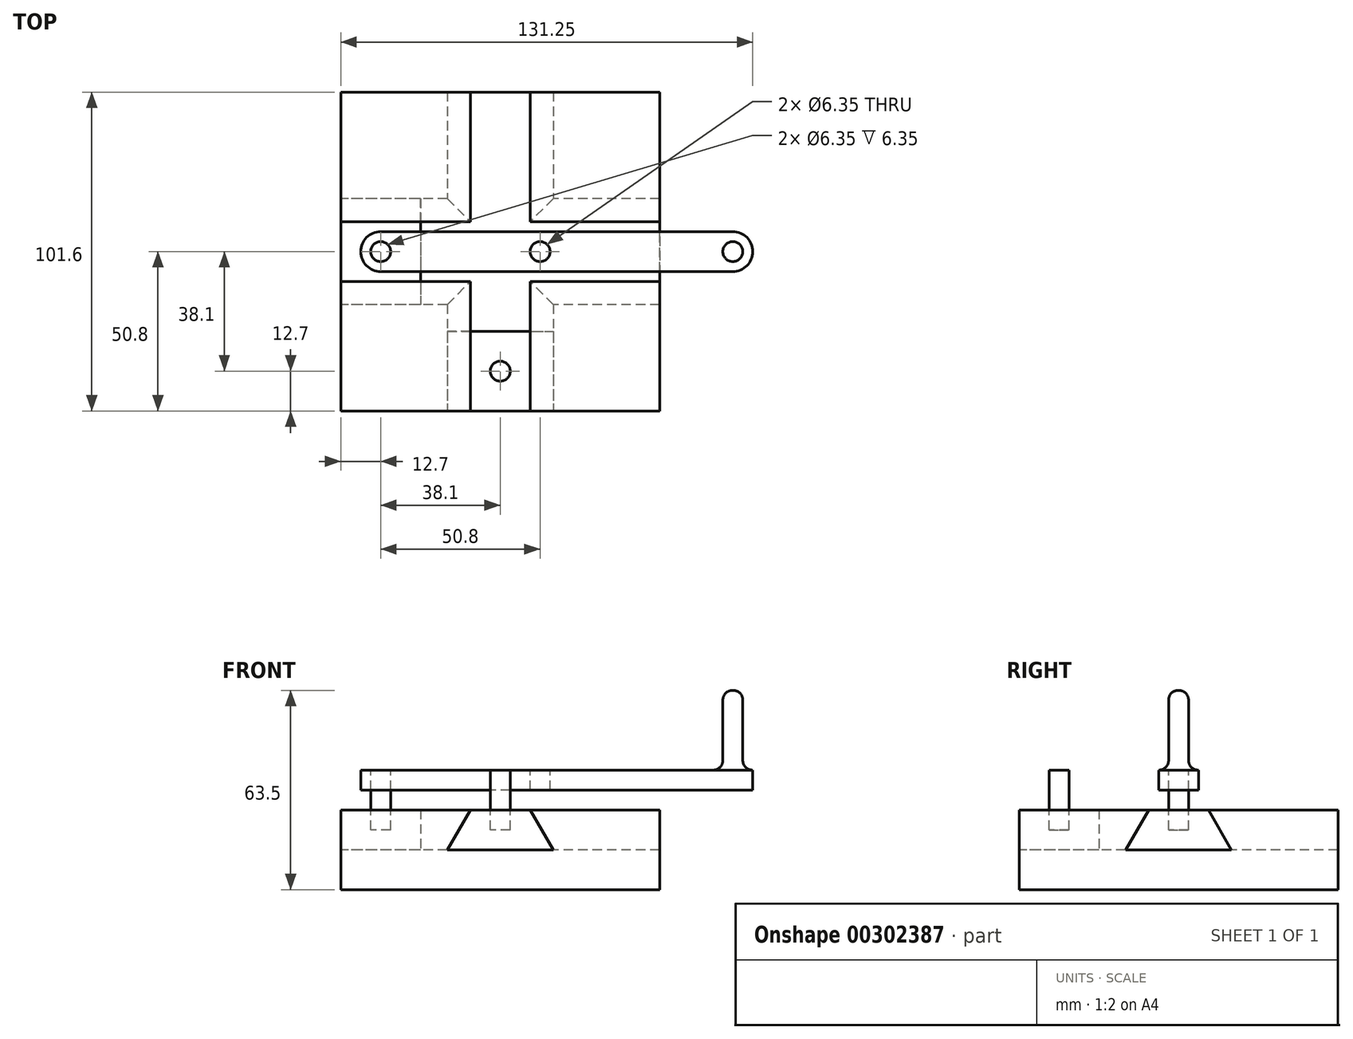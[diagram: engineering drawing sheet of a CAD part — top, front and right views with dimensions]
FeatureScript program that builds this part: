
annotation { "Feature Type Name" : "Feature", "Feature Type Description" : "" }
export const myFeature = defineFeature(function(context is Context, id is Id, definition is map)
    precondition{}
    {
        {
            var Q0;
            Q0=qCreatedBy(makeId("Top.planeOp"),FACE);
            var sketch = newSketch(context, id + "F0", { "sketchPlane" : qUnion([Q0])});
            skLineSegment(sketch, "E0", {"start": v(0, 50.8) * mm, "end": v(-50.8, 50.8) * mm});
            skLineSegment(sketch, "E1", {"start": v(-50.8, 50.8) * mm, "end": v(-50.8, 0) * mm});
            skLineSegment(sketch, "E2", {"start": v(-50.8, 0) * mm, "end": v(-50.8, -50.8) * mm});
            skLineSegment(sketch, "E3", {"start": v(-50.8, -50.8) * mm, "end": v(0, -50.8) * mm});
            skLineSegment(sketch, "E4", {"start": v(0, -50.8) * mm, "end": v(50.8, -50.8) * mm});
            skLineSegment(sketch, "E5", {"start": v(50.8, 50.8) * mm, "end": v(0, 50.8) * mm});
            skLineSegment(sketch, "E6", {"start": v(50.8, 50.8) * mm, "end": v(50.8, 0) * mm});
            skLineSegment(sketch, "E7", {"start": v(50.8, 0) * mm, "end": v(50.8, -50.8) * mm});
            skSolve(sketch);
        }
        {
            var Q0;
            Q0=makeQuery(id+"F0.imprint","IMPRINT",FACE,{"disambiguationData":[TD([[makeQuery(id+"F0.imprint","IMPRINT",EDGE,{"derivedFrom":sQuery(id+"F0.wireOp",EDGE,"E0")}),1.0]])]});
            extrude(context, id + "F1", {"entities" : qUnion([Q0]), "depth" : 25.4 * mm});
        }
        {
            var Q0;
            Q0=makeQuery(id+"F1.opExtrude","SWEPT_FACE",FACE,{"disambiguationData":[OSD([sQuery(id+"F0.wireOp",EDGE,"E1"),sQuery(id+"F0.wireOp",EDGE,"E2")])]});
            var sketch = newSketch(context, id + "F2", { "sketchPlane" : qUnion([Q0])});
            skLineSegment(sketch, "E8", {"start": v(-50.8, 12.7) * mm, "end": v(50.8, 12.7) * mm});
            skLineSegment(sketch, "E9", {"start": v(0, 25.4) * mm, "end": v(-9.52, 25.4) * mm});
            skLineSegment(sketch, "E10", {"start": v(-9.52, 25.4) * mm, "end": v(9.53, 25.4) * mm});
            skLineSegment(sketch, "E11", {"start": v(-9.52, 25.4) * mm, "end": v(-16.86, 12.7) * mm});
            skLineSegment(sketch, "E12", {"start": v(9.53, 25.4) * mm, "end": v(16.86, 12.7) * mm});
            skSolve(sketch);
        }
        {
            var Q0;
            {var subQ0=sQuery(id+"F2.wireOp",EDGE,"E11");Q0=makeQuery(id+"F2.imprint","IMPRINT",FACE,{"disambiguationData":[TD([[makeQuery(id+"F2.imprint","IMPRINT",EDGE,{"derivedFrom":subQ0}),1.0]])]});}
            extrude(context, id + "F3", {"entities" : qUnion([Q0]), "operationType" : NewBodyOperationType.REMOVE, "endBound" : BoundingType.THROUGH_ALL, "oppositeDirection" : true, "depth" : 25.4 * mm});
        }
        {
            var Q0;
            Q0=makeQuery(id+"F1.opExtrude","SWEPT_FACE",FACE,{"disambiguationData":[OSD([sQuery(id+"F0.wireOp",EDGE,"E3"),sQuery(id+"F0.wireOp",EDGE,"E4")])]});
            var sketch = newSketch(context, id + "F4", { "sketchPlane" : qUnion([Q0])});
            skSolve(sketch);
        }
        {
            var Q0;
            {var subQ0=sQuery(id+"F0.wireOp",EDGE,"E3");Q0=makeQuery(id+"F4.imprint","IMPRINT",FACE,{"disambiguationData":[TD([[makeQuery(id+"F4.imprint","IMPRINT",EDGE,{"derivedFrom":makeQuery(id+"F1.opExtrude","SWEPT_EDGE",EDGE,{"disambiguationData":[OSD([sQuery(id+"F0.wireOp",EDGE,"E2"),subQ0])]})}),1.0]])]});}
            var sketch = newSketch(context, id + "F5", { "sketchPlane" : qUnion([Q0])});
            skLineSegment(sketch, "E13", {"start": v(-50.8, 12.7) * mm, "end": v(50.8, 12.7) * mm});
            skLineSegment(sketch, "E14", {"start": v(0, 25.4) * mm, "end": v(0, 0) * mm, "construction": true});
            skLineSegment(sketch, "E15", {"start": v(0, 25.4) * mm, "end": v(-9.53, 25.4) * mm});
            skLineSegment(sketch, "E16", {"start": v(0, 25.4) * mm, "end": v(9.53, 25.4) * mm});
            skLineSegment(sketch, "E17", {"start": v(-9.52, 25.4) * mm, "end": v(-16.86, 12.7) * mm});
            skLineSegment(sketch, "E18", {"start": v(9.52, 25.4) * mm, "end": v(16.86, 12.7) * mm});
            skSolve(sketch);
        }
        {
            var Q0;
            Q0=makeQuery(id+"F5.imprint","IMPRINT",FACE,{"disambiguationData":[TD([[makeQuery(id+"F5.imprint","IMPRINT",EDGE,{"derivedFrom":sQuery(id+"F5.wireOp",EDGE,"E15")}),-1.0]])]});
            extrude(context, id + "F6", {"entities" : qUnion([Q0]), "operationType" : NewBodyOperationType.REMOVE, "endBound" : BoundingType.THROUGH_ALL, "oppositeDirection" : true, "depth" : 25.4 * mm});
        }
        {
            var Q0;
            Q0=makeQuery(id+"F5.imprint","IMPRINT",FACE,{"disambiguationData":[TD([[makeQuery(id+"F5.imprint","IMPRINT",EDGE,{"derivedFrom":sQuery(id+"F5.wireOp",EDGE,"E15")}),-1.0]])]});
            extrude(context, id + "F7", {"entities" : qUnion([Q0]), "oppositeDirection" : true, "depth" : 25.4 * mm});
        }
        {
            var Q0;
            Q0 = qSketchRegion(id + "F2", true);
            extrude(context, id + "F8", {"entities" : qUnion([Q0]), "oppositeDirection" : true, "depth" : 25.4 * mm});
        }
        {
            var Q0;
            Q0=makeQuery(id+"F8.opExtrude","SWEPT_FACE",FACE,{"disambiguationData":[OSD([sQuery(id+"F2.wireOp",EDGE,"E10")])]});
            var sketch = newSketch(context, id + "F9", { "sketchPlane" : qUnion([Q0])});
            skLineSegment(sketch, "E19", {"start": v(-50.8, 9.52) * mm, "end": v(-25.4, -9.53) * mm, "construction": true});
            skLineSegment(sketch, "E20", {"start": v(-50.8, -9.53) * mm, "end": v(-25.4, 9.52) * mm, "construction": true});
            skCircle(sketch, "E21", {"center": v(-38.1, 0) * mm, "radius": 3.18 * mm});
            skSolve(sketch);
        }
        {
            var Q0;
            Q0=makeQuery(id+"F9.imprint","IMPRINT",FACE,{"disambiguationData":[TD([[makeQuery(id+"F9.imprint","IMPRINT",EDGE,{"derivedFrom":sQuery(id+"F9.wireOp",EDGE,"E21")}),1.0]])]});
            extrude(context, id + "F10", {"entities" : qUnion([Q0]), "operationType" : NewBodyOperationType.REMOVE, "oppositeDirection" : true, "depth" : 6.35 * mm});
        }
        {
            var Q0;
            Q0 = qSketchRegion(id + "F9", true);
            extrude(context, id + "F11", {"entities" : qUnion([Q0]), "operationType" : NewBodyOperationType.ADD, "depth" : 12.7 * mm});
        }
        {
            var Q0;
            Q0=makeQuery(id+"F7.opExtrude","SWEPT_FACE",FACE,{"disambiguationData":[OSD([sQuery(id+"F5.wireOp",EDGE,"E15"),sQuery(id+"F5.wireOp",EDGE,"E16")])]});
            var sketch = newSketch(context, id + "F12", { "sketchPlane" : qUnion([Q0])});
            skLineSegment(sketch, "E22", {"start": v(-9.53, -25.4) * mm, "end": v(9.53, -50.8) * mm, "construction": true});
            skLineSegment(sketch, "E23", {"start": v(9.53, -25.4) * mm, "end": v(-9.53, -50.8) * mm, "construction": true});
            skCircle(sketch, "E24", {"center": v(0, -38.1) * mm, "radius": 3.18 * mm});
            skSolve(sketch);
        }
        {
            var Q0;
            Q0=makeQuery(id+"F12.imprint","IMPRINT",FACE,{"disambiguationData":[TD([[makeQuery(id+"F12.imprint","IMPRINT",EDGE,{"derivedFrom":sQuery(id+"F12.wireOp",EDGE,"E24")}),1.0]])]});
            var Q1;
            Q1 = qConstructionFilter(qBodyType(qCreatedBy(id + "F12" ,EDGE), BodyType.WIRE), ConstructionObject.NO);
            extrude(context, id + "F13", {"entities" : qUnion([Q0]), "operationType" : NewBodyOperationType.REMOVE, "surfaceEntities" : qUnion([Q1]), "oppositeDirection" : true, "depth" : 6.35 * mm});
        }
        {
            var Q0;
            Q0=makeQuery(id+"F12.imprint","IMPRINT",FACE,{"disambiguationData":[TD([[makeQuery(id+"F12.imprint","IMPRINT",EDGE,{"derivedFrom":sQuery(id+"F12.wireOp",EDGE,"E24")}),1.0]])]});
            var Q1;
            Q1=sQuery(id+"F12.wireOp",EDGE,"E24");
            extrude(context, id + "F14", {"entities" : qUnion([Q0]), "operationType" : NewBodyOperationType.ADD, "surfaceEntities" : qUnion([Q1]), "depth" : 12.7 * mm});
        }
        {
            var Q0;
            Q0=makeQuery(id+"F14.opExtrude","CAP_FACE",FACE,{"disambiguationData":[OSD([sQuery(id+"F12.wireOp",EDGE,"E24")])],"isStart":false});
            var sketch = newSketch(context, id + "F15", { "sketchPlane" : qUnion([Q0])});
            skCircle(sketch, "E25", {"center": v(-38.1, 0) * mm, "radius": 6.35 * mm});
            skLineSegment(sketch, "E26", {"start": v(-38.1, 0) * mm, "end": v(38.3, 0) * mm, "construction": true});
            skCircle(sketch, "E27", {"center": v(-38.1, 0) * mm, "radius": 3.18 * mm});
            skLineSegment(sketch, "E28", {"start": v(0, 0) * mm, "end": v(12.7, 0) * mm});
            skCircle(sketch, "E29", {"center": v(12.7, 0) * mm, "radius": 6.35 * mm});
            skCircle(sketch, "E30", {"center": v(12.7, 0) * mm, "radius": 3.18 * mm});
            skLineSegment(sketch, "E31", {"start": v(-38.1, 6.35) * mm, "end": v(12.7, 6.35) * mm});
            skLineSegment(sketch, "E32", {"start": v(12.7, 6.35) * mm, "end": v(74.1, 6.35) * mm});
            skLineSegment(sketch, "E33", {"start": v(74.1, 6.35) * mm, "end": v(74.1, -6.35) * mm, "construction": true});
            skLineSegment(sketch, "E34", {"start": v(74.1, -6.35) * mm, "end": v(12.7, -6.35) * mm});
            skLineSegment(sketch, "E35", {"start": v(12.7, -6.35) * mm, "end": v(-38.1, -6.35) * mm});
            skCircle(sketch, "E36", {"center": v(74.1, 0) * mm, "radius": 6.35 * mm});
            skCircle(sketch, "E37", {"center": v(74.1, 0) * mm, "radius": 3.18 * mm});
            skSolve(sketch);
        }
        {
            var Q0;
            {var subQ0=sQuery(id+"F15.wireOp",EDGE,"WmhgMogH-GQ3H-kHXB-snts-v6sjiJhQ2gga");var subQ1=makeQuery(id+"F15.imprint","INTERSECT",VERTEX,{"derivedFrom":[sQuery(id+"F15.wireOp",EDGE,"TYPQlNbo-xgLa-Lmpp-WkNG-PMnZoqi9gQiG"),subQ0]});Q0=makeQuery(id+"F15.imprint","IMPRINT",FACE,{"disambiguationData":[TD([[makeQuery(id+"F15.imprint","IMPRINT",EDGE,{"disambiguationData":[TD([[subQ1,1.0]])],"derivedFrom":subQ0}),1.0]])]});}
            var Q1;
            {var subQ0=sQuery(id+"F15.wireOp",EDGE,"ym3YC1Lw-J6GC-uMcu-XXUQ-S2R32xc2RU5x");Q1=makeQuery(id+"F15.imprint","IMPRINT",FACE,{"disambiguationData":[TD([[makeQuery(id+"F15.imprint","IMPRINT",EDGE,{"derivedFrom":subQ0}),1.0]])]});}
            var Q2;
            {var subQ0=sQuery(id+"F15.wireOp",EDGE,"TYPQlNbo-xgLa-Lmpp-WkNG-PMnZoqi9gQiG");var subQ5=sQuery(id+"F15.wireOp",EDGE,"WmhgMogH-GQ3H-kHXB-snts-v6sjiJhQ2gga");var subQ6=makeQuery(id+"F15.imprint","INTERSECT",VERTEX,{"derivedFrom":[subQ0,subQ5]});Q2=makeQuery(id+"F15.imprint","IMPRINT",FACE,{"disambiguationData":[TD([[makeQuery(id+"F15.imprint","IMPRINT",EDGE,{"disambiguationData":[TD([[subQ6,1.0]])],"derivedFrom":subQ5}),-1.0]])]});}
            var Q3;
            Q3=makeQuery(id+"F15.imprint","IMPRINT",FACE,{"disambiguationData":[TD([[makeQuery(id+"F15.imprint","IMPRINT",EDGE,{"derivedFrom":makeQuery(id+"F14.opExtrude","CAP_EDGE",EDGE,{"disambiguationData":[OSD([sQuery(id+"F12.wireOp",EDGE,"E24")])],"isStart":false})}),-1.0]])]});
            var Q4;
            {var subQ0=sQuery(id+"F15.wireOp",EDGE,"E25");var subQ1=makeQuery(id+"F15.imprint","INTERSECT",VERTEX,{"derivedFrom":[subQ0,sQuery(id+"F15.wireOp",EDGE,"ym3YC1Lw-J6GC-uMcu-XXUQ-S2R32xc2RU5x")]});Q4=makeQuery(id+"F15.imprint","IMPRINT",FACE,{"disambiguationData":[TD([[makeQuery(id+"F15.imprint","IMPRINT",EDGE,{"disambiguationData":[TD([[subQ1,1.0]])],"derivedFrom":subQ0}),1.0]])]});}
            var Q5;
            {var subQ0=sQuery(id+"F15.wireOp",EDGE,"E31");Q5=makeQuery(id+"F15.imprint","IMPRINT",FACE,{"disambiguationData":[TD([[makeQuery(id+"F15.imprint","IMPRINT",EDGE,{"derivedFrom":subQ0}),-1.0]])]});}
            var Q6;
            {var subQ0=sQuery(id+"F15.wireOp",EDGE,"E32");Q6=makeQuery(id+"F15.imprint","IMPRINT",FACE,{"disambiguationData":[TD([[makeQuery(id+"F15.imprint","IMPRINT",EDGE,{"derivedFrom":subQ0}),-1.0]])]});}
            var Q7;
            Q7=makeQuery(id+"F15.imprint","IMPRINT",FACE,{"disambiguationData":[TD([[makeQuery(id+"F15.imprint","IMPRINT",EDGE,{"derivedFrom":sQuery(id+"F15.wireOp",EDGE,"E30")}),-1.0]])]});
            var Q8;
            Q8=makeQuery(id+"F15.imprint","IMPRINT",FACE,{"disambiguationData":[TD([[makeQuery(id+"F15.imprint","IMPRINT",EDGE,{"derivedFrom":sQuery(id+"F15.wireOp",EDGE,"E37")}),-1.0]])]});
            var Q9;
            Q9=makeQuery(id+"F15.imprint","IMPRINT",FACE,{"disambiguationData":[TD([[makeQuery(id+"F15.imprint","IMPRINT",EDGE,{"derivedFrom":sQuery(id+"F15.wireOp",EDGE,"E37")}),1.0]])]});
            extrude(context, id + "F16", {"entities" : qUnion([Q0, Q1, Q2, Q3, Q4, Q5, Q6, Q7, Q8, Q9]), "oppositeDirection" : true, "depth" : 6.35 * mm});
        }
        {
            var Q0;
            Q0=makeQuery(id+"F15.imprint","IMPRINT",FACE,{"disambiguationData":[TD([[makeQuery(id+"F15.imprint","IMPRINT",EDGE,{"derivedFrom":sQuery(id+"F15.wireOp",EDGE,"E37")}),1.0]])]});
            var Q1;
            Q1=sQuery(id+"F15.wireOp",EDGE,"E37");
            extrude(context, id + "F17", {"entities" : qUnion([Q0]), "operationType" : NewBodyOperationType.ADD, "surfaceEntities" : qUnion([Q1]), "depth" : 25.4 * mm});
        }
        {
            var Q0;
            Q0=makeQuery(id+"F17.opExtrude","CAP_FACE",FACE,{"disambiguationData":[OSD([sQuery(id+"F15.wireOp",EDGE,"E37")])],"isStart":false});
            var Q1;
            Q1=makeQuery(id+"F17.opExtrude","SWEPT_FACE",FACE,{"disambiguationData":[OSD([sQuery(id+"F15.wireOp",EDGE,"E37")])]});
            fillet(context, id + "F18", {"entities" : qUnion([Q0, Q1]), "radius" : 3.05 * mm, "tangentPropagation" : true, "allowEdgeOverflow" : false});
        }
    });
